# Revit family: PRD_AR_PprTwlDpnsrs_RODANPaperTowelDispenser_RODX600
name_source: partatom
category: Furniture
revit_build: Autodesk Revit 2018 (Build: 20190510_1515(x64)
units: mm (PartAtom-declared; Revit-internal decimal feet)

## family parameters
Cut with Voids When Loaded = No
Host = Face
OmniClass Number = 23.40.20.21
OmniClass Title = Toilet and Bath Specialties
Room Calculation Point = No
Shared = No

## types (1)
- RODX600
    AssetType = Fixed
    BIMObjectName = PRD_AR_PaperTowelDispensers_RODANPaperTowelDispenser_RODX600
    Category = Pr_40_70_22_62, Paper towel dispensers
    Color = Stainless steel
    Default Elevation = 1200 mm
    Description = Paper towel dispenser for wall mounting, stainless steel, surface satin finished, material thickness 0.8 mm, folded front cover, cylinder lock with KWC standard key, inspection windows on sides, loading capacity 300 - 400 pcs. of paper depending on convolution, incl. stainless steel screws and dowels.
    DispenserMaterial = PRD_AR_StainlessSteel_SatinFinished
    DurationUnit = year
    Features = stainless steel, 0.80 mm, satin finished, wall mounting, 275x355x112 mm (WxHxD)
    Finish = Satin finished
    Form = Wall mounted
    GrossWeight = 2.57 kg
    IfcExportAs = IfcFurnitureType
    IfcExportType = NOTDEFINED
    IntegralAccessories = Stainless steel screws and dowels incl.
    MainColor = Stainless steel
    Manufacturer = KWC Group AG
    ManufacturerName = KWC Group AG
    ManufacturerURL = www.kwc.com
    Material = Stainless steel
    MaterialsBody = Stainless steel
    MaterialsFinishAndColour = Stainless steel, satin finished
    Model = RODX600
    ModelNumber = 2000090056
    ModelReference = RODX600
    NBSDescription = Paper towel dispensers
    NBSReference = 45-35-72/344
    Name = RODAN paper towel dispenser RODX600
    NetWeight = 2.13 kg
    NominalDepth = 112 mm  [stored 0.367454 ft]
    NominalHeight = 355 mm  [stored 1.1647 ft]
    NominalLength = 275 mm
    NominalWidth = 275 mm
    Operation = Manual
    OverallDepth = 112 mm  [stored 0.367454 ft]
    OverallHeight = 355 mm  [stored 1.1647 ft]
    OverallWidth = 275 mm
    ProductInformation = https://pim.kwc.com
    Size = 275x355x112 mm
    Style = Paper towel dispenser
    TowelsWidth = 0 mm  [stored 0 ft]
    TypeOfConsumable = Paper towel
    URL = www.kwc.com
    Uniclass2015Code = Pr_40_70_22_62
    Uniclass2015Title = Paper towel dispensers
    Uniclass2015Version = Products v1.7
    Version = 1
    WarrantyDurationUnit = year

note: [stored X ft] marks values corroborated as IEEE doubles in the binary element streams (Revit-internal decimal feet)

## geometry (parser evidence)
native form markers: Sweep x2
no freeform markers — native parametric forms only
